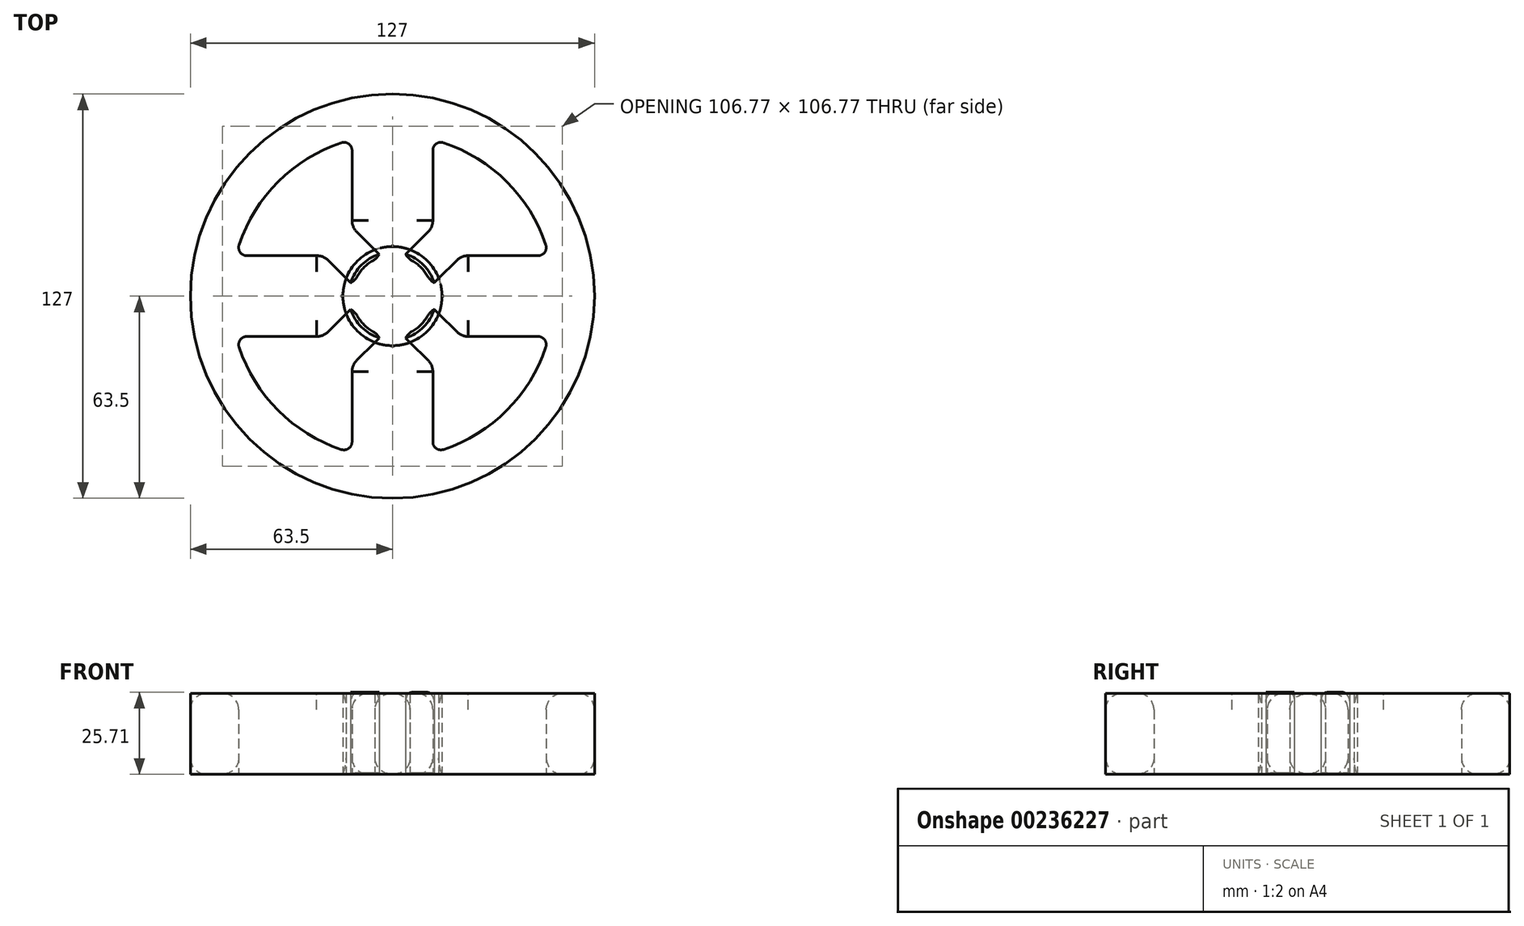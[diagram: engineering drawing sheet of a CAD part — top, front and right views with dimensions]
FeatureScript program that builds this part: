
annotation { "Feature Type Name" : "Feature", "Feature Type Description" : "" }
export const myFeature = defineFeature(function(context is Context, id is Id, definition is map)
    precondition{}
    {
        {
            var Q0;
            Q0=qCreatedBy(makeId("Top.planeOp"),FACE);
            var sketch = newSketch(context, id + "F0", { "sketchPlane" : qUnion([Q0])});
            skArc(sketch, "E0", {"start": v(-16.04, 48.2) * mm, "mid": v(-35.92, 35.92) * mm, "end": v(-48.2, 16.04) * mm});
            skCircle(sketch, "E1", {"center": v(0, 0) * mm, "radius": 63.5 * mm});
            skCircle(sketch, "E2", {"center": v(0, 0) * mm, "radius": 12.7 * mm});
            skLineSegment(sketch, "E3", {"start": v(0, 0) * mm, "end": v(0, 50.8) * mm});
            skLineSegment(sketch, "E4.0", {"start": v(-12.7, 21.68) * mm, "end": v(-12.7, 45.8) * mm});
            skLineSegment(sketch, "E5.0", {"start": v(12.7, 21.68) * mm, "end": v(12.7, 45.8) * mm});
            skLineSegment(sketch, "E6", {"start": v(0, 0) * mm, "end": v(0, -50.8) * mm});
            skLineSegment(sketch, "E7", {"start": v(0, 0) * mm, "end": v(50.8, 0) * mm});
            skLineSegment(sketch, "E8", {"start": v(0, 0) * mm, "end": v(-12.7, 0) * mm});
            skLineSegment(sketch, "E9.0", {"start": v(21.68, -12.7) * mm, "end": v(45.8, -12.7) * mm});
            skLineSegment(sketch, "E10.0", {"start": v(21.68, 12.7) * mm, "end": v(45.8, 12.7) * mm});
            skLineSegment(sketch, "E11.0", {"start": v(-21.68, 12.7) * mm, "end": v(-45.8, 12.7) * mm});
            skLineSegment(sketch, "E12.0", {"start": v(-21.68, -12.7) * mm, "end": v(-45.8, -12.7) * mm});
            skLineSegment(sketch, "E13.0", {"start": v(-12.7, -21.68) * mm, "end": v(-12.7, -45.8) * mm});
            skLineSegment(sketch, "E14.0", {"start": v(12.7, -21.68) * mm, "end": v(12.7, -45.8) * mm});
            skArc(sketch, "E15.trimOffspring", {"start": v(48.2, 16.04) * mm, "mid": v(35.92, 35.92) * mm, "end": v(16.04, 48.2) * mm});
            skArc(sketch, "E16.trimOffspring", {"start": v(-48.2, -16.04) * mm, "mid": v(-35.92, -35.92) * mm, "end": v(-16.04, -48.2) * mm});
            skArc(sketch, "E17.trimOffspring", {"start": v(16.04, -48.2) * mm, "mid": v(35.92, -35.92) * mm, "end": v(48.2, -16.04) * mm});
            skLineSegment(sketch, "E18", {"start": v(0, 0) * mm, "end": v(-50.25, 0) * mm});
            skPoint(sketch, "E19.visualSharp", {"position": v(-12.7, 12.7) * mm});
            skPoint(sketch, "E20.visualSharp", {"position": v(12.7, 12.7) * mm});
            skPoint(sketch, "E21.visualSharp", {"position": v(12.7, -12.7) * mm});
            skPoint(sketch, "E22.visualSharp", {"position": v(-12.7, -12.7) * mm});
            skPoint(sketch, "E23.visualSharp", {"position": v(-49.19, 12.7) * mm});
            skArc(sketch, "E23.filletArc", {"start": v(-48.2, 16.04) * mm, "mid": v(-47.85, 13.75) * mm, "end": v(-45.8, 12.7) * mm});
            skPoint(sketch, "E24.visualSharp", {"position": v(-12.7, 49.19) * mm});
            skArc(sketch, "E24.filletArc", {"start": v(-12.7, 45.8) * mm, "mid": v(-13.75, 47.85) * mm, "end": v(-16.04, 48.2) * mm});
            skPoint(sketch, "E25.visualSharp", {"position": v(12.7, 49.19) * mm});
            skArc(sketch, "E25.filletArc", {"start": v(16.04, 48.2) * mm, "mid": v(13.75, 47.85) * mm, "end": v(12.7, 45.8) * mm});
            skPoint(sketch, "E26.visualSharp", {"position": v(49.19, 12.7) * mm});
            skArc(sketch, "E26.filletArc", {"start": v(45.8, 12.7) * mm, "mid": v(47.85, 13.75) * mm, "end": v(48.2, 16.04) * mm});
            skPoint(sketch, "E27.visualSharp", {"position": v(49.19, -12.7) * mm});
            skArc(sketch, "E27.filletArc", {"start": v(48.2, -16.04) * mm, "mid": v(47.85, -13.75) * mm, "end": v(45.8, -12.7) * mm});
            skPoint(sketch, "E28.visualSharp", {"position": v(12.7, -49.19) * mm});
            skArc(sketch, "E28.filletArc", {"start": v(12.7, -45.8) * mm, "mid": v(13.75, -47.85) * mm, "end": v(16.04, -48.2) * mm});
            skPoint(sketch, "E29.visualSharp", {"position": v(-12.7, -49.19) * mm});
            skArc(sketch, "E29.filletArc", {"start": v(-16.04, -48.2) * mm, "mid": v(-13.75, -47.85) * mm, "end": v(-12.7, -45.8) * mm});
            skPoint(sketch, "E30.visualSharp", {"position": v(-49.19, -12.7) * mm});
            skArc(sketch, "E30.filletArc", {"start": v(-45.8, -12.7) * mm, "mid": v(-47.85, -13.75) * mm, "end": v(-48.2, -16.04) * mm});
            skLineSegment(sketch, "E31.0", {"start": v(12.27, -3.29) * mm, "end": v(21.68, -12.7) * mm});
            skLineSegment(sketch, "E32.0", {"start": v(-3.29, 12.27) * mm, "end": v(-12.7, 21.68) * mm});
            skLineSegment(sketch, "E33.0", {"start": v(-12.27, 3.29) * mm, "end": v(-21.68, 12.7) * mm});
            skLineSegment(sketch, "E34.0", {"start": v(12.27, 3.29) * mm, "end": v(21.68, 12.7) * mm});
            skLineSegment(sketch, "E35.0", {"start": v(3.29, 12.27) * mm, "end": v(12.7, 21.68) * mm});
            skLineSegment(sketch, "E36.0", {"start": v(-12.27, -3.29) * mm, "end": v(-21.68, -12.7) * mm});
            skLineSegment(sketch, "E37.0", {"start": v(-3.29, -12.27) * mm, "end": v(-12.7, -21.68) * mm});
            skLineSegment(sketch, "E38.trimOffspring", {"start": v(-31.15, 40.13) * mm, "end": v(-31.43, 40.41) * mm});
            skLineSegment(sketch, "E39.trimOffspring", {"start": v(-40.13, 31.15) * mm, "end": v(-40.41, 31.43) * mm});
            skLineSegment(sketch, "E40.trimOffspring", {"start": v(31.15, 40.13) * mm, "end": v(31.43, 40.41) * mm});
            skPoint(sketch, "E41.orphan", {"position": v(35.92, 35.92) * mm});
            skLineSegment(sketch, "E42.trimOffspring", {"start": v(40.13, 31.15) * mm, "end": v(40.41, 31.43) * mm});
            skLineSegment(sketch, "E43.trimOffspring", {"start": v(40.13, -31.15) * mm, "end": v(40.41, -31.43) * mm});
            skPoint(sketch, "E44.orphan", {"position": v(35.92, -35.92) * mm});
            skLineSegment(sketch, "E45.trimOffspring", {"start": v(31.15, -40.13) * mm, "end": v(31.43, -40.41) * mm});
            skLineSegment(sketch, "E46.trimOffspring", {"start": v(-31.15, -40.13) * mm, "end": v(-31.43, -40.41) * mm});
            skPoint(sketch, "E47.orphan", {"position": v(-35.92, -35.92) * mm});
            skLineSegment(sketch, "E48.trimOffspring", {"start": v(-40.13, -31.15) * mm, "end": v(-40.41, -31.43) * mm});
            skPoint(sketch, "E49.orphan", {"position": v(-35.92, 35.92) * mm});
            skLineSegment(sketch, "E50.0", {"start": v(3.29, -12.27) * mm, "end": v(12.7, -21.68) * mm});
            skCircle(sketch, "E51", {"center": v(0, 0) * mm, "radius": 13.79 * mm});
            skCircle(sketch, "E52", {"center": v(0, 0) * mm, "radius": 15.57 * mm});
            skSolve(sketch);
        }
        {
            var Q0;
            Q0 = qSketchRegion(id + "F0", true);
            extrude(context, id + "F1", {"entities" : qUnion([Q0]), "depth" : 25.4 * mm});
        }
        {
            var Q0;
            Q0 = qSketchRegion(id + "F0", true);
            extrude(context, id + "F2", {"entities" : qUnion([Q0]), "operationType" : NewBodyOperationType.ADD, "depth" : 25.4 * mm});
        }
        {
            var Q0;
            {var subQ0=sQuery(id+"F0.wireOp",EDGE,"E34.0");var subQ1=sQuery(id+"F0.wireOp",EDGE,"E2");var subQ2=makeQuery(id+"F0.imprint","INTERSECT",VERTEX,{"derivedFrom":[subQ1,subQ0]});Q0=makeQuery(id+"F0.imprint","IMPRINT",FACE,{"disambiguationData":[TD([[makeQuery(id+"F0.imprint","IMPRINT",EDGE,{"disambiguationData":[TD([[subQ2,-1.0]])],"derivedFrom":subQ1}),-1.0]])]});}
            var Q1;
            {var subQ0=sQuery(id+"F0.wireOp",EDGE,"E32.0");var subQ1=sQuery(id+"F0.wireOp",EDGE,"E2");var subQ2=makeQuery(id+"F0.imprint","INTERSECT",VERTEX,{"derivedFrom":[subQ1,subQ0]});Q1=makeQuery(id+"F0.imprint","IMPRINT",FACE,{"disambiguationData":[TD([[makeQuery(id+"F0.imprint","IMPRINT",EDGE,{"disambiguationData":[TD([[subQ2,-1.0]])],"derivedFrom":subQ1}),-1.0]])]});}
            var Q2;
            {var subQ0=sQuery(id+"F0.wireOp",EDGE,"E36.0");var subQ1=sQuery(id+"F0.wireOp",EDGE,"E2");var subQ2=makeQuery(id+"F0.imprint","INTERSECT",VERTEX,{"derivedFrom":[subQ1,subQ0]});Q2=makeQuery(id+"F0.imprint","IMPRINT",FACE,{"disambiguationData":[TD([[makeQuery(id+"F0.imprint","IMPRINT",EDGE,{"disambiguationData":[TD([[subQ2,-1.0]])],"derivedFrom":subQ1}),-1.0]])]});}
            var Q3;
            {var subQ0=sQuery(id+"F0.wireOp",EDGE,"E31.0");var subQ1=sQuery(id+"F0.wireOp",EDGE,"E2");var subQ2=makeQuery(id+"F0.imprint","INTERSECT",VERTEX,{"derivedFrom":[subQ1,subQ0]});Q3=makeQuery(id+"F0.imprint","IMPRINT",FACE,{"disambiguationData":[TD([[makeQuery(id+"F0.imprint","IMPRINT",EDGE,{"disambiguationData":[TD([[subQ2,1.0]])],"derivedFrom":subQ1}),-1.0]])]});}
            extrude(context, id + "F3", {"entities" : qUnion([Q0, Q1, Q2, Q3]), "depth" : 25.71 * mm, "hasSecondDirection" : true, "secondDirectionOppositeDirection" : false, "secondDirectionDepth" : 0.4 * mm});
        }
        {
            var Q0;
            Q0=makeQuery(id+"F1.opExtrude","SWEPT_EDGE",EDGE,{"disambiguationData":[OSD([sQuery(id+"F0.wireOp",EDGE,"E4.0"),sQuery(id+"F0.wireOp",EDGE,"E32.0")])]});
            fillet(context, id + "F4", {"entities" : qUnion([Q0]), "radius" : 5.08 * mm, "tangentPropagation" : true, "allowEdgeOverflow" : false});
        }
        {
            var Q0;
            Q0=makeQuery(id+"F1.opExtrude","SWEPT_EDGE",EDGE,{"disambiguationData":[OSD([sQuery(id+"F0.wireOp",EDGE,"E11.0"),sQuery(id+"F0.wireOp",EDGE,"E33.0")])]});
            fillet(context, id + "F5", {"entities" : qUnion([Q0]), "radius" : 5.08 * mm, "tangentPropagation" : true, "allowEdgeOverflow" : false});
        }
        {
            var Q0;
            Q0=makeQuery(id+"F3.opExtrude","SWEPT_EDGE",EDGE,{"disambiguationData":[OSD([sQuery(id+"F0.wireOp",EDGE,"E2"),sQuery(id+"F0.wireOp",EDGE,"E36.0")])]});
            fillet(context, id + "F6", {"entities" : qUnion([Q0]), "radius" : 5.08 * mm, "tangentPropagation" : true, "allowEdgeOverflow" : false});
        }
        {
            var Q0;
            Q0=makeQuery(id+"F3.opExtrude","SWEPT_EDGE",EDGE,{"disambiguationData":[OSD([sQuery(id+"F0.wireOp",EDGE,"E2"),sQuery(id+"F0.wireOp",EDGE,"E37.0")])]});
            fillet(context, id + "F7", {"entities" : qUnion([Q0]), "radius" : 5.08 * mm, "tangentPropagation" : true, "allowEdgeOverflow" : false});
        }
        {
            var Q0;
            Q0=makeQuery(id+"F3.opExtrude","SWEPT_EDGE",EDGE,{"disambiguationData":[OSD([sQuery(id+"F0.wireOp",EDGE,"E2"),sQuery(id+"F0.wireOp",EDGE,"E32.0")])]});
            fillet(context, id + "F8", {"entities" : qUnion([Q0]), "radius" : 5.08 * mm, "tangentPropagation" : true, "allowEdgeOverflow" : false});
        }
        {
            var Q0;
            Q0=makeQuery(id+"F3.opExtrude","SWEPT_EDGE",EDGE,{"disambiguationData":[OSD([sQuery(id+"F0.wireOp",EDGE,"E2"),sQuery(id+"F0.wireOp",EDGE,"E34.0")])]});
            fillet(context, id + "F9", {"entities" : qUnion([Q0]), "radius" : 5.08 * mm, "tangentPropagation" : true, "allowEdgeOverflow" : false});
        }
        {
            var Q0;
            Q0=makeQuery(id+"F3.opExtrude","SWEPT_EDGE",EDGE,{"disambiguationData":[OSD([sQuery(id+"F0.wireOp",EDGE,"E2"),sQuery(id+"F0.wireOp",EDGE,"E35.0")])]});
            fillet(context, id + "F10", {"entities" : qUnion([Q0]), "radius" : 5.08 * mm, "tangentPropagation" : true, "allowEdgeOverflow" : false});
        }
        {
            var Q0;
            Q0=makeQuery(id+"F3.opExtrude","SWEPT_EDGE",EDGE,{"disambiguationData":[OSD([sQuery(id+"F0.wireOp",EDGE,"E2"),sQuery(id+"F0.wireOp",EDGE,"E50.0")])]});
            fillet(context, id + "F11", {"entities" : qUnion([Q0]), "radius" : 5.08 * mm, "tangentPropagation" : true, "allowEdgeOverflow" : false});
        }
        {
            var Q0;
            Q0=makeQuery(id+"F3.opExtrude","SWEPT_EDGE",EDGE,{"disambiguationData":[OSD([sQuery(id+"F0.wireOp",EDGE,"E2"),sQuery(id+"F0.wireOp",EDGE,"E31.0")])]});
            fillet(context, id + "F12", {"entities" : qUnion([Q0]), "radius" : 5.08 * mm, "tangentPropagation" : true, "allowEdgeOverflow" : false});
        }
        {
            var Q0;
            Q0=makeQuery(id+"F1.opExtrude","SWEPT_EDGE",EDGE,{"disambiguationData":[OSD([sQuery(id+"F0.wireOp",EDGE,"E5.0"),sQuery(id+"F0.wireOp",EDGE,"E35.0")])]});
            fillet(context, id + "F13", {"entities" : qUnion([Q0]), "radius" : 5.08 * mm, "tangentPropagation" : true, "allowEdgeOverflow" : false});
        }
        {
            var Q0;
            Q0=makeQuery(id+"F1.opExtrude","SWEPT_EDGE",EDGE,{"disambiguationData":[OSD([sQuery(id+"F0.wireOp",EDGE,"E9.0"),sQuery(id+"F0.wireOp",EDGE,"E31.0")])]});
            fillet(context, id + "F14", {"entities" : qUnion([Q0]), "radius" : 5.08 * mm, "tangentPropagation" : true, "allowEdgeOverflow" : false});
        }
        {
            var Q0;
            Q0=makeQuery(id+"F1.opExtrude","SWEPT_EDGE",EDGE,{"disambiguationData":[OSD([sQuery(id+"F0.wireOp",EDGE,"E14.0"),sQuery(id+"F0.wireOp",EDGE,"E50.0")])]});
            fillet(context, id + "F15", {"entities" : qUnion([Q0]), "radius" : 5.08 * mm, "tangentPropagation" : true, "allowEdgeOverflow" : false});
        }
        {
            var Q0;
            Q0=makeQuery(id+"F1.opExtrude","SWEPT_EDGE",EDGE,{"disambiguationData":[OSD([sQuery(id+"F0.wireOp",EDGE,"E10.0"),sQuery(id+"F0.wireOp",EDGE,"E34.0")])]});
            fillet(context, id + "F16", {"entities" : qUnion([Q0]), "radius" : 5.08 * mm, "tangentPropagation" : true, "allowEdgeOverflow" : false});
        }
        {
            var Q0;
            Q0=makeQuery(id+"F1.opExtrude","SWEPT_EDGE",EDGE,{"disambiguationData":[OSD([sQuery(id+"F0.wireOp",EDGE,"E12.0"),sQuery(id+"F0.wireOp",EDGE,"E36.0")])]});
            fillet(context, id + "F17", {"entities" : qUnion([Q0]), "radius" : 5.08 * mm, "tangentPropagation" : true, "allowEdgeOverflow" : false});
        }
        {
            var Q0;
            Q0=makeQuery(id+"F1.opExtrude","SWEPT_EDGE",EDGE,{"disambiguationData":[OSD([sQuery(id+"F0.wireOp",EDGE,"E13.0"),sQuery(id+"F0.wireOp",EDGE,"E37.0")])]});
            fillet(context, id + "F18", {"entities" : qUnion([Q0]), "radius" : 5.08 * mm, "tangentPropagation" : true, "allowEdgeOverflow" : false});
        }
        {
            var Q0;
            Q0=makeQuery(id+"F1.opExtrude","CAP_EDGE",EDGE,{"disambiguationData":[OSD([sQuery(id+"F0.wireOp",EDGE,"E11.0")])],"isStart":true});
            fillet(context, id + "F19", {"entities" : qUnion([Q0]), "radius" : 5.08 * mm, "tangentPropagation" : true, "allowEdgeOverflow" : false});
        }
        {
            var Q0;
            Q0=makeQuery(id+"F1.opExtrude","CAP_EDGE",EDGE,{"disambiguationData":[OSD([sQuery(id+"F0.wireOp",EDGE,"E13.0")])],"isStart":true});
            fillet(context, id + "F20", {"entities" : qUnion([Q0]), "radius" : 5.08 * mm, "tangentPropagation" : true, "allowEdgeOverflow" : false});
        }
        {
            var Q0;
            Q0=makeQuery(id+"F1.opExtrude","CAP_EDGE",EDGE,{"disambiguationData":[OSD([sQuery(id+"F0.wireOp",EDGE,"E5.0")])],"isStart":true});
            fillet(context, id + "F21", {"entities" : qUnion([Q0]), "radius" : 5.08 * mm, "tangentPropagation" : true, "allowEdgeOverflow" : false});
        }
        {
            var Q0;
            Q0=makeQuery(id+"F1.opExtrude","CAP_EDGE",EDGE,{"disambiguationData":[OSD([sQuery(id+"F0.wireOp",EDGE,"E9.0")])],"isStart":true});
            fillet(context, id + "F22", {"entities" : qUnion([Q0]), "radius" : 5.08 * mm, "tangentPropagation" : true, "allowEdgeOverflow" : false});
        }
        {
            var Q0;
            Q0=makeQuery(id+"F1.opExtrude","CAP_EDGE",EDGE,{"disambiguationData":[OSD([sQuery(id+"F0.wireOp",EDGE,"E9.0")])],"isStart":false});
            fillet(context, id + "F23", {"entities" : qUnion([Q0]), "radius" : 5.08 * mm, "tangentPropagation" : true, "allowEdgeOverflow" : false});
        }
        {
            var Q0;
            Q0=makeQuery(id+"F1.opExtrude","CAP_EDGE",EDGE,{"disambiguationData":[OSD([sQuery(id+"F0.wireOp",EDGE,"E15.trimOffspring")])],"isStart":false});
            fillet(context, id + "F24", {"entities" : qUnion([Q0]), "radius" : 5.08 * mm, "tangentPropagation" : true, "allowEdgeOverflow" : false});
        }
        {
            var Q0;
            Q0=makeQuery(id+"F1.opExtrude","CAP_EDGE",EDGE,{"disambiguationData":[OSD([sQuery(id+"F0.wireOp",EDGE,"E0")])],"isStart":false});
            fillet(context, id + "F25", {"entities" : qUnion([Q0]), "radius" : 5.08 * mm, "tangentPropagation" : true, "allowEdgeOverflow" : false});
        }
        {
            var Q0;
            Q0=makeQuery(id+"F1.opExtrude","CAP_EDGE",EDGE,{"disambiguationData":[OSD([sQuery(id+"F0.wireOp",EDGE,"E16.trimOffspring")])],"isStart":false});
            fillet(context, id + "F26", {"entities" : qUnion([Q0]), "radius" : 5.08 * mm, "tangentPropagation" : true, "allowEdgeOverflow" : false});
        }
        {
            var Q0;
            Q0=makeQuery(id+"F3.opExtrude","SWEPT_EDGE",EDGE,{"disambiguationData":[OSD([sQuery(id+"F0.wireOp",EDGE,"E2"),sQuery(id+"F0.wireOp",EDGE,"E33.0")])]});
            fillet(context, id + "F27", {"entities" : qUnion([Q0]), "radius" : 5.08 * mm, "tangentPropagation" : true, "allowEdgeOverflow" : false});
        }
        {
            var Q0;
            {var subQ0=sQuery(id+"F0.wireOp",EDGE,"E51");Q0=makeQuery(id+"F3.opExtrude","CAP_EDGE",EDGE,{"disambiguationData":[OSD([subQ0]),TDD([makeQuery(id+"F0.imprint","IMPRINT",EDGE,{"disambiguationData":[TD([[makeQuery(id+"F0.imprint","INTERSECT",VERTEX,{"derivedFrom":[sQuery(id+"F0.wireOp",EDGE,"E32.0"),subQ0]}),-1.0]])],"derivedFrom":subQ0})])],"isStart":false});}
            fillet(context, id + "F28", {"entities" : qUnion([Q0]), "radius" : 5.08 * mm, "tangentPropagation" : true, "allowEdgeOverflow" : false});
        }
        {
            var Q0;
            {var subQ0=sQuery(id+"F0.wireOp",EDGE,"E51");Q0=makeQuery(id+"F3.opExtrude","CAP_EDGE",EDGE,{"disambiguationData":[OSD([subQ0]),TDD([makeQuery(id+"F0.imprint","IMPRINT",EDGE,{"disambiguationData":[TD([[makeQuery(id+"F0.imprint","INTERSECT",VERTEX,{"derivedFrom":[sQuery(id+"F0.wireOp",EDGE,"E31.0"),subQ0]}),1.0]])],"derivedFrom":subQ0})])],"isStart":false});}
            fillet(context, id + "F29", {"entities" : qUnion([Q0]), "radius" : 5.08 * mm, "tangentPropagation" : true, "allowEdgeOverflow" : false});
        }
        {
            var Q0;
            {var subQ0=sQuery(id+"F0.wireOp",EDGE,"E51");Q0=makeQuery(id+"F3.opExtrude","CAP_EDGE",EDGE,{"disambiguationData":[OSD([subQ0]),TDD([makeQuery(id+"F0.imprint","IMPRINT",EDGE,{"disambiguationData":[TD([[makeQuery(id+"F0.imprint","INTERSECT",VERTEX,{"derivedFrom":[sQuery(id+"F0.wireOp",EDGE,"E34.0"),subQ0]}),-1.0]])],"derivedFrom":subQ0})])],"isStart":false});}
            fillet(context, id + "F30", {"entities" : qUnion([Q0]), "radius" : 5.08 * mm, "tangentPropagation" : true, "allowEdgeOverflow" : false});
        }
        {
            var Q0;
            Q0 = qSketchRegion(id + "F0", true);
            var Q1;
            {var subQ0=sQuery(id+"F0.wireOp",EDGE,"E51");var subQ1=sQuery(id+"F0.wireOp",EDGE,"E36.0");var subQ2=makeQuery(id+"F0.imprint","INTERSECT",VERTEX,{"derivedFrom":[subQ1,subQ0]});Q1=makeQuery(id+"F0.imprint","IMPRINT",FACE,{"disambiguationData":[TD([[makeQuery(id+"F0.imprint","IMPRINT",EDGE,{"disambiguationData":[TD([[subQ2,-1.0]])],"derivedFrom":subQ1}),1.0]])]});}
            var Q2;
            {var subQ0=sQuery(id+"F0.wireOp",EDGE,"E51");var subQ1=sQuery(id+"F0.wireOp",EDGE,"E31.0");var subQ2=makeQuery(id+"F0.imprint","INTERSECT",VERTEX,{"derivedFrom":[subQ1,subQ0]});Q2=makeQuery(id+"F0.imprint","IMPRINT",FACE,{"disambiguationData":[TD([[makeQuery(id+"F0.imprint","IMPRINT",EDGE,{"disambiguationData":[TD([[subQ2,-1.0]])],"derivedFrom":subQ1}),-1.0]])]});}
            var Q3;
            {var subQ0=sQuery(id+"F0.wireOp",EDGE,"E51");var subQ1=sQuery(id+"F0.wireOp",EDGE,"E34.0");var subQ2=makeQuery(id+"F0.imprint","INTERSECT",VERTEX,{"derivedFrom":[subQ1,subQ0]});Q3=makeQuery(id+"F0.imprint","IMPRINT",FACE,{"disambiguationData":[TD([[makeQuery(id+"F0.imprint","IMPRINT",EDGE,{"disambiguationData":[TD([[subQ2,-1.0]])],"derivedFrom":subQ1}),1.0]])]});}
            var Q4;
            {var subQ0=sQuery(id+"F0.wireOp",EDGE,"E51");var subQ1=sQuery(id+"F0.wireOp",EDGE,"E32.0");var subQ2=makeQuery(id+"F0.imprint","INTERSECT",VERTEX,{"derivedFrom":[subQ1,subQ0]});Q4=makeQuery(id+"F0.imprint","IMPRINT",FACE,{"disambiguationData":[TD([[makeQuery(id+"F0.imprint","IMPRINT",EDGE,{"disambiguationData":[TD([[subQ2,-1.0]])],"derivedFrom":subQ1}),1.0]])]});}
            extrude(context, id + "F31", {"entities" : qUnion([Q0, Q1, Q2, Q3, Q4]), "depth" : 25.4 * mm});
        }
        {
            var Q0;
            Q0=makeQuery(id+"F31.opExtrude","CAP_EDGE",EDGE,{"disambiguationData":[OSD([sQuery(id+"F0.wireOp",EDGE,"E0")])],"isStart":false});
            fillet(context, id + "F32", {"entities" : qUnion([Q0]), "radius" : 5.08 * mm, "tangentPropagation" : true, "allowEdgeOverflow" : false});
        }
        {
            var Q0;
            Q0=makeQuery(id+"F31.opExtrude","CAP_EDGE",EDGE,{"disambiguationData":[OSD([sQuery(id+"F0.wireOp",EDGE,"E16.trimOffspring")])],"isStart":false});
            fillet(context, id + "F33", {"entities" : qUnion([Q0]), "radius" : 5.08 * mm, "tangentPropagation" : true, "allowEdgeOverflow" : false});
        }
        {
            var Q0;
            Q0=makeQuery(id+"F31.opExtrude","CAP_EDGE",EDGE,{"disambiguationData":[OSD([sQuery(id+"F0.wireOp",EDGE,"E15.trimOffspring")])],"isStart":false});
            fillet(context, id + "F34", {"entities" : qUnion([Q0]), "radius" : 5.08 * mm, "tangentPropagation" : true, "allowEdgeOverflow" : false});
        }
        {
            var Q0;
            Q0=makeQuery(id+"F31.opExtrude","CAP_EDGE",EDGE,{"disambiguationData":[OSD([sQuery(id+"F0.wireOp",EDGE,"E17.trimOffspring")])],"isStart":false});
            fillet(context, id + "F35", {"entities" : qUnion([Q0]), "radius" : 5.08 * mm, "tangentPropagation" : true, "allowEdgeOverflow" : false});
        }
        {
            var Q0;
            Q0=makeQuery(id+"F31.opExtrude","SWEPT_EDGE",EDGE,{"disambiguationData":[OSD([sQuery(id+"F0.wireOp",EDGE,"E11.0"),sQuery(id+"F0.wireOp",EDGE,"E33.0")])]});
            fillet(context, id + "F36", {"entities" : qUnion([Q0]), "radius" : 5.08 * mm, "tangentPropagation" : true, "allowEdgeOverflow" : false});
        }
        {
            var Q0;
            Q0=makeQuery(id+"F31.opExtrude","SWEPT_EDGE",EDGE,{"disambiguationData":[OSD([sQuery(id+"F0.wireOp",EDGE,"E4.0"),sQuery(id+"F0.wireOp",EDGE,"E32.0")])]});
            fillet(context, id + "F37", {"entities" : qUnion([Q0]), "radius" : 5.08 * mm, "tangentPropagation" : true, "allowEdgeOverflow" : false});
        }
        {
            var Q0;
            Q0=makeQuery(id+"F31.opExtrude","SWEPT_EDGE",EDGE,{"disambiguationData":[OSD([sQuery(id+"F0.wireOp",EDGE,"E5.0"),sQuery(id+"F0.wireOp",EDGE,"E35.0")])]});
            fillet(context, id + "F38", {"entities" : qUnion([Q0]), "radius" : 5.08 * mm, "tangentPropagation" : true, "allowEdgeOverflow" : false});
        }
        {
            var Q0;
            Q0=makeQuery(id+"F31.opExtrude","SWEPT_EDGE",EDGE,{"disambiguationData":[OSD([sQuery(id+"F0.wireOp",EDGE,"E10.0"),sQuery(id+"F0.wireOp",EDGE,"E34.0")])]});
            fillet(context, id + "F39", {"entities" : qUnion([Q0]), "radius" : 5.08 * mm, "tangentPropagation" : true, "allowEdgeOverflow" : false});
        }
        {
            var Q0;
            {var subQ0=sQuery(id+"F0.wireOp",EDGE,"E31.0");var subQ1=sQuery(id+"F0.wireOp",EDGE,"E9.0");Q0=makeQuery(id+"F35.opFillet","BLEND_EDGE",EDGE,{"blendedFrom":[makeQuery(id+"F31.opExtrude","CAP_EDGE",EDGE,{"disambiguationData":[OSD([subQ1])],"isStart":false}),makeQuery(id+"F31.opExtrude","SWEPT_FACE",FACE,{"disambiguationData":[OSD([subQ0]),TDD([makeQuery(id+"F0.imprint","IMPRINT",EDGE,{"disambiguationData":[TD([[makeQuery(id+"F0.imprint","INTERSECT",VERTEX,{"derivedFrom":[subQ1,subQ0]}),1.0]])],"derivedFrom":subQ0})])]})],"blendedInto":[makeQuery(id+"F31.opExtrude","SWEPT_FACE",FACE,{"disambiguationData":[OSD([subQ0]),TDD([makeQuery(id+"F0.imprint","IMPRINT",EDGE,{"disambiguationData":[TD([[makeQuery(id+"F0.imprint","INTERSECT",VERTEX,{"derivedFrom":[subQ1,subQ0]}),1.0]])],"derivedFrom":subQ0})])]})]});}
            fillet(context, id + "F40", {"entities" : qUnion([Q0]), "radius" : 5.08 * mm, "tangentPropagation" : true, "allowEdgeOverflow" : false});
        }
        {
            var Q0;
            Q0=makeQuery(id+"F31.opExtrude","SWEPT_EDGE",EDGE,{"disambiguationData":[OSD([sQuery(id+"F0.wireOp",EDGE,"E14.0"),sQuery(id+"F0.wireOp",EDGE,"E50.0")])]});
            fillet(context, id + "F41", {"entities" : qUnion([Q0]), "radius" : 5.08 * mm, "tangentPropagation" : true, "allowEdgeOverflow" : false});
        }
        {
            var Q0;
            Q0=makeQuery(id+"F31.opExtrude","SWEPT_EDGE",EDGE,{"disambiguationData":[OSD([sQuery(id+"F0.wireOp",EDGE,"E13.0"),sQuery(id+"F0.wireOp",EDGE,"E37.0")])]});
            fillet(context, id + "F42", {"entities" : qUnion([Q0]), "radius" : 5.08 * mm, "tangentPropagation" : true, "allowEdgeOverflow" : false});
        }
        {
            var Q0;
            Q0=makeQuery(id+"F31.opExtrude","SWEPT_EDGE",EDGE,{"disambiguationData":[OSD([sQuery(id+"F0.wireOp",EDGE,"E12.0"),sQuery(id+"F0.wireOp",EDGE,"E36.0")])]});
            fillet(context, id + "F43", {"entities" : qUnion([Q0]), "radius" : 5.08 * mm, "tangentPropagation" : true, "allowEdgeOverflow" : false});
        }
        {
            var Q0;
            Q0=makeQuery(id+"F1.opExtrude","SWEPT_FACE",FACE,{"disambiguationData":[OSD([sQuery(id+"F0.wireOp",EDGE,"E1")])]});
            fillet(context, id + "F44", {"entities" : qUnion([Q0]), "radius" : 5.08 * mm, "tangentPropagation" : true, "allowEdgeOverflow" : false});
        }
    });
